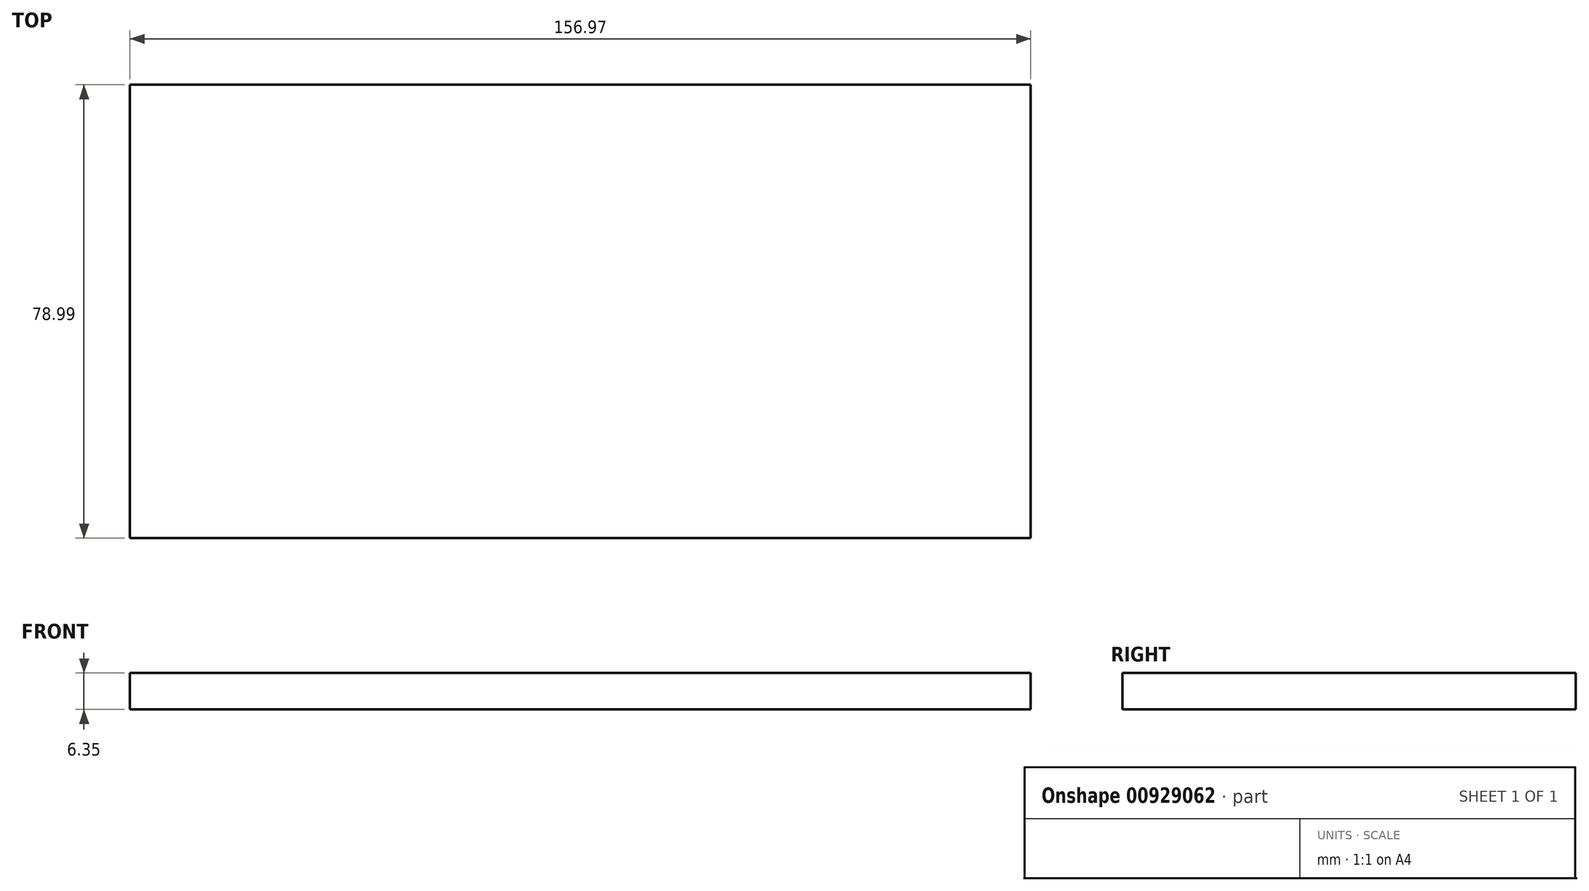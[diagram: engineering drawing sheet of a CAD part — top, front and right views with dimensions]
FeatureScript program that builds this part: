
annotation { "Feature Type Name" : "Feature", "Feature Type Description" : "" }
export const myFeature = defineFeature(function(context is Context, id is Id, definition is map)
    precondition{}
    {
        {
            var Q0;
            Q0=qCreatedBy(makeId("Top.planeOp"),FACE);
            var sketch = newSketch(context, id + "F0", { "sketchPlane" : qUnion([Q0])});
            skLineSegment(sketch, "E0.bottom", {"start": v(0, 0) * mm, "end": v(156.97, 0) * mm});
            skLineSegment(sketch, "E0.top", {"start": v(0, -79) * mm, "end": v(156.97, -79) * mm});
            skLineSegment(sketch, "E0.left", {"start": v(0, 0) * mm, "end": v(0, -79) * mm});
            skLineSegment(sketch, "E0.right", {"start": v(156.97, 0) * mm, "end": v(156.97, -79) * mm});
            skSolve(sketch);
        }
        {
            var Q0;
            Q0=makeQuery(id+"F0.imprint","IMPRINT",FACE,{"disambiguationData":[TD([[makeQuery(id+"F0.imprint","IMPRINT",EDGE,{"derivedFrom":sQuery(id+"F0.wireOp",EDGE,"E0.bottom")}),-1.0]])]});
            extrude(context, id + "F1", {"entities" : qUnion([Q0]), "depth" : 6.35 * mm, "offsetDistance" : 25.4 * mm});
        }
    });
